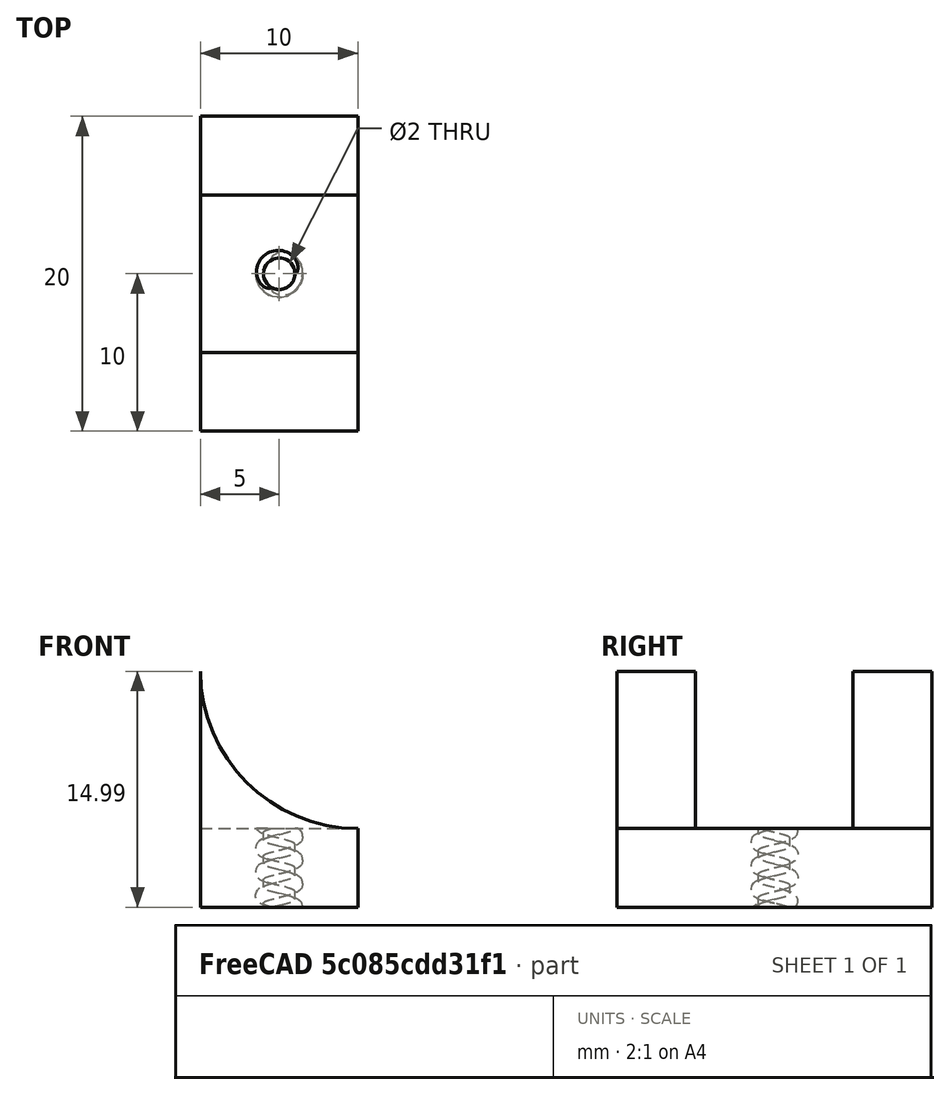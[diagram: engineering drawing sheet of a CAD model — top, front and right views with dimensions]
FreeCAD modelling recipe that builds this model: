
FCSTD DOCUMENT  (FreeCAD 0.21R33694 (Git))
Label: acople-flotador
License: Creative Commons Attribution-NonCommercial-ShareAlike 4.0
LicenseURL: https://creativecommons.org/licenses/by-nc-sa/4.0/
objects: Part::Box×4, Part::Cut×4, Part::Fuse×1, Part::Fillet×1, Part::Cylinder×1, Part::Feature×1
note: 12 computed .brp shape members not serialized (recipe doc carries the construction recipe); baked Part::Feature solids carry a one-line shape summary decoded from their .brp

FEATURE [Part::Box] Box  label="Cube"
  AttacherType = Attacher::AttachEngine3D
  Height = 5
  Length = 10
  Width = 20
FEATURE [Part::Box] Box001  label="Cube001"
  AttacherType = Attacher::AttachEngine3D
  Height = 50
  Length = 5
  Placement = pos=(-5,0,0) rot=(0,0,1;0rad)
  Width = 20
FEATURE [Part::Fuse] Fusion
  Base = -> Box
  Refine = true
  Tool = -> Box001
FEATURE [Part::Fillet] Fillet
  Base = -> Fusion
  Edges = 1 edges r=9.99: [Edge5]
FEATURE [Part::Box] Box002  label="Cube002"
  AttacherType = Attacher::AttachEngine3D
  Height = 50
  Length = 5
  Placement = pos=(-5,0,0) rot=(0,0,1;0rad)
  Width = 20
FEATURE [Part::Cut] Cut
  Base = -> Fillet
  Refine = true
  Tool = -> Box002
FEATURE [Part::Box] Box003  label="Cube003"
  AttacherType = Attacher::AttachEngine3D
  Height = 20
  Length = 10
  Placement = pos=(0,5,5) rot=(0,0,1;0rad)
  Width = 10
FEATURE [Part::Cut] Cut001
  Base = -> Cut
  Refine = true
  Tool = -> Box003
FEATURE [Part::Cylinder] Cylinder
  Angle = 360
  AttacherType = Attacher::AttachEngine3D
  FirstAngle = 0
  Height = 6
  Placement = pos=(5,10,0) rot=(0,0,1;0rad)
  Radius = 0.5
  SecondAngle = 0
FEATURE [Part::Cut] Cut002  label="acople"
  Base = -> Cut001
  Refine = true
  Tool = -> Cylinder
FEATURE [Part::Feature] Fusion001001  label="Rosca macho002"
  Placement = pos=(5,10,-9) rot=(0,0,1;0rad)
  shape: bbox 3.919 x 4.387 x 44 mm, 35 faces (baked)
FEATURE [Part::Cut] Cut003  label="acople-roscado"
  Base = -> Cut002
  Refine = true
  Tool = -> Fusion001001
